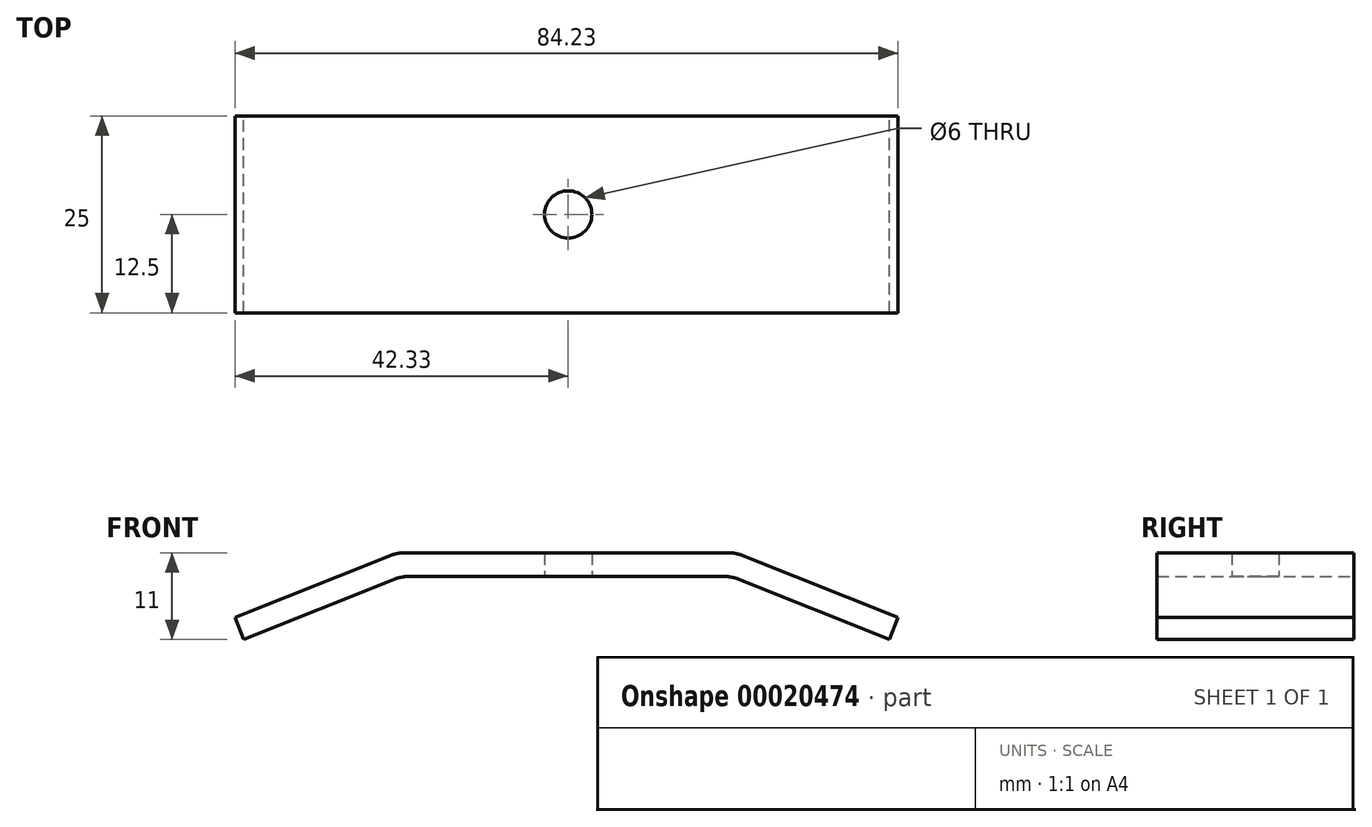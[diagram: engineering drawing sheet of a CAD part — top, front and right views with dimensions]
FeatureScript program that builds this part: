
annotation { "Feature Type Name" : "Feature", "Feature Type Description" : "" }
export const myFeature = defineFeature(function(context is Context, id is Id, definition is map)
    precondition{}
    {
        {
            var Q0;
            Q0=qCreatedBy(makeId("Front.planeOp"),FACE);
            var sketch = newSketch(context, id + "F0", { "sketchPlane" : qUnion([Q0])});
            skLineSegment(sketch, "E0", {"start": v(-42.33, -19.68) * mm, "end": v(-21.8, -11.47) * mm});
            skLineSegment(sketch, "E1", {"start": v(-21.8, -11.47) * mm, "end": v(21.36, -11.47) * mm});
            skLineSegment(sketch, "E2", {"start": v(21.36, -11.47) * mm, "end": v(41.9, -19.68) * mm});
            skLineSegment(sketch, "E3", {"start": v(41.9, -19.68) * mm, "end": v(40.78, -22.47) * mm});
            skLineSegment(sketch, "E4", {"start": v(40.78, -22.47) * mm, "end": v(20.78, -14.47) * mm});
            skLineSegment(sketch, "E5", {"start": v(20.78, -14.47) * mm, "end": v(-21.22, -14.47) * mm});
            skLineSegment(sketch, "E6", {"start": v(-21.22, -14.47) * mm, "end": v(-41.22, -22.47) * mm});
            skLineSegment(sketch, "E7", {"start": v(-41.22, -22.47) * mm, "end": v(-42.33, -19.68) * mm});
            skSolve(sketch);
        }
        {
            var Q0;
            Q0=makeQuery(id+"F0.imprint","IMPRINT",FACE,{"disambiguationData":[TD([[makeQuery(id+"F0.imprint","IMPRINT",EDGE,{"derivedFrom":sQuery(id+"F0.wireOp",EDGE,"E0")}),-1.0]])]});
            extrude(context, id + "F1", {"entities" : qUnion([Q0]), "depth" : 25 * mm});
        }
        {
            var Q0;
            Q0=makeQuery(id+"F1.opExtrude","SWEPT_FACE",FACE,{"disambiguationData":[OSD([sQuery(id+"F0.wireOp",EDGE,"E1")])]});
            var sketch = newSketch(context, id + "F2", { "sketchPlane" : qUnion([Q0])});
            skPoint(sketch, "E8", {"position": v(0, -12.5) * mm});
            skSolve(sketch);
        }
        {
            var Q0;
            Q0=sQuery(id+"F2.wireOp",VERTEX,"E8");
            var Q1;
            Q1=makeQuery(id+"F1.opExtrude","SWEPT_BODY",BODY,{"disambiguationData":[OSD([sQuery(id+"F0.wireOp",EDGE,"E0"),sQuery(id+"F0.wireOp",EDGE,"E1"),sQuery(id+"F0.wireOp",EDGE,"E2"),sQuery(id+"F0.wireOp",EDGE,"E3"),sQuery(id+"F0.wireOp",EDGE,"E4"),sQuery(id+"F0.wireOp",EDGE,"E5"),sQuery(id+"F0.wireOp",EDGE,"E6"),sQuery(id+"F0.wireOp",EDGE,"E7")])]});
            hole(context, id + "F3", {"style" : HoleStyle.SIMPLE, "holeDiameter" : 6 * mm, "endStyle" : HoleEndStyle.THROUGH, "locations" : qUnion([Q0]), "scope" : qUnion([Q1])});
        }
        {
            var Q0;
            Q0=makeQuery(id+"F1.opExtrude","SWEPT_EDGE",EDGE,{"disambiguationData":[OSD([sQuery(id+"F0.wireOp",EDGE,"E5"),sQuery(id+"F0.wireOp",EDGE,"E6")])]});
            var Q1;
            Q1=makeQuery(id+"F1.opExtrude","SWEPT_EDGE",EDGE,{"disambiguationData":[OSD([sQuery(id+"F0.wireOp",EDGE,"E4"),sQuery(id+"F0.wireOp",EDGE,"E5")])]});
            fillet(context, id + "F4", {"entities" : qUnion([Q0, Q1]), "radius" : 5 * mm, "tangentPropagation" : true, "allowEdgeOverflow" : false});
        }
        {
            var Q0;
            Q0=makeQuery(id+"F1.opExtrude","SWEPT_EDGE",EDGE,{"disambiguationData":[OSD([sQuery(id+"F0.wireOp",EDGE,"E0"),sQuery(id+"F0.wireOp",EDGE,"E1")])]});
            var Q1;
            Q1=makeQuery(id+"F1.opExtrude","SWEPT_EDGE",EDGE,{"disambiguationData":[OSD([sQuery(id+"F0.wireOp",EDGE,"E1"),sQuery(id+"F0.wireOp",EDGE,"E2")])]});
            fillet(context, id + "F5", {"entities" : qUnion([Q0, Q1]), "radius" : 5 * mm, "tangentPropagation" : true, "allowEdgeOverflow" : false});
        }
    });
